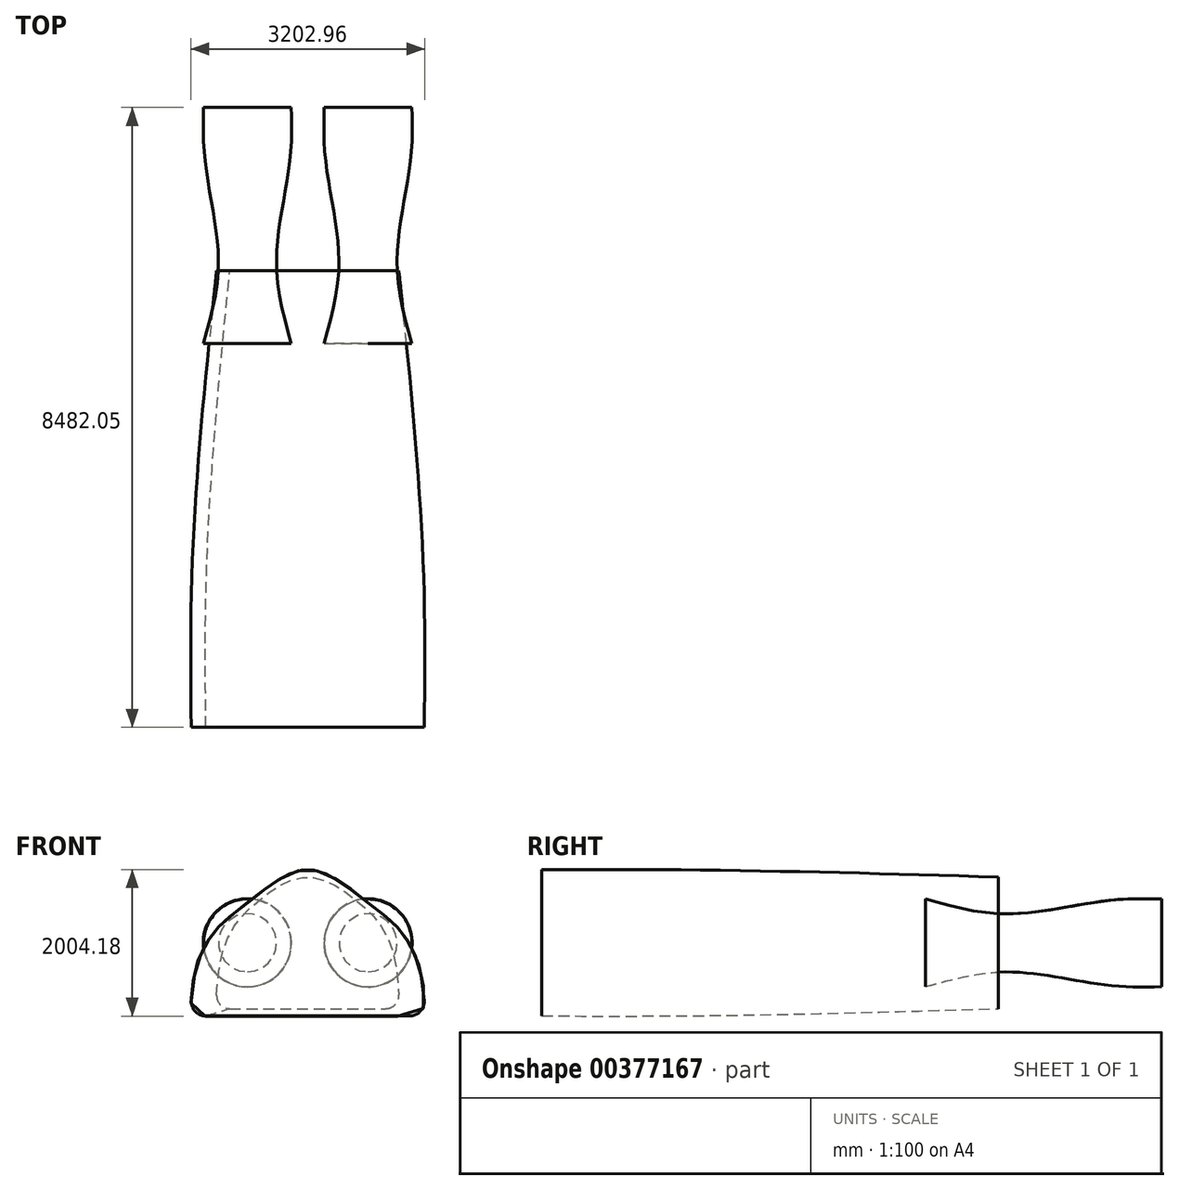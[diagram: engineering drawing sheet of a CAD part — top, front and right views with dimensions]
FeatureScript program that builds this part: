
annotation { "Feature Type Name" : "Feature", "Feature Type Description" : "" }
export const myFeature = defineFeature(function(context is Context, id is Id, definition is map)
    precondition{}
    {
        {
            var Q0;
            Q0=qCreatedBy(makeId("Front.planeOp"),FACE);
            cPlane(context, id + "F0", {"entities" : qUnion([Q0]), "cplaneType" : CPlaneType.OFFSET, "offset" : 1750 * mm, "width" : 150 * mm, "height" : 150 * mm});
        }
        {
            var Q0;
            Q0=qCreatedBy(id+"F0.planeOp",FACE);
            var sketch = newSketch(context, id + "F1", { "sketchPlane" : qUnion([Q0])});
            skLineSegment(sketch, "E0.top", {"start": v(-1394.2, -1000) * mm, "end": v(1394.2, -1000) * mm});
            skPoint(sketch, "E0.middle", {"position": v(0, 0) * mm});
            skFitSpline(sketch, "E1", {"points": [v(-1600, -1000) * mm, v(-848, 530) * mm, v(0, 1000) * mm, v(848, 530) * mm, v(1600, -1000) * mm], "startDerivative": vector(0, 10524.75) * mm, "endDerivative": vector(0, -10524.75) * mm});
            skArc(sketch, "E2.filletArc", {"start": v(-1593.82, -787.83) * mm, "mid": v(-1539.85, -937.05) * mm, "end": v(-1394.2, -1000) * mm});
            skArc(sketch, "E3.filletArc", {"start": v(1394.2, -1000) * mm, "mid": v(1539.85, -937.05) * mm, "end": v(1593.82, -787.83) * mm});
            skSolve(sketch);
        }
        {
            var Q0;
            Q0=qCreatedBy(makeId("Front.planeOp"),FACE);
            var sketch = newSketch(context, id + "F2", { "sketchPlane" : qUnion([Q0])});
            skLineSegment(sketch, "E4.top", {"start": v(-1394.2, -1000) * mm, "end": v(1394.2, -1000) * mm});
            skPoint(sketch, "E4.middle", {"position": v(0, 0) * mm});
            skFitSpline(sketch, "E5", {"points": [v(-1600, -1000) * mm, v(-848, 530) * mm, v(0, 1000) * mm, v(848, 530) * mm, v(1600, -1000) * mm], "startDerivative": vector(0, 10524.75) * mm, "endDerivative": vector(0, -10524.75) * mm});
            skArc(sketch, "E6.filletArc", {"start": v(-1593.82, -787.83) * mm, "mid": v(-1539.85, -937.05) * mm, "end": v(-1394.2, -1000) * mm});
            skArc(sketch, "E7.filletArc", {"start": v(1394.2, -1000) * mm, "mid": v(1539.85, -937.05) * mm, "end": v(1593.82, -787.83) * mm});
            skSolve(sketch);
        }
        {
            var Q0;
            Q0=qCreatedBy(makeId("Front.planeOp"),FACE);
            cPlane(context, id + "F3", {"entities" : qUnion([Q0]), "cplaneType" : CPlaneType.OFFSET, "offset" : 3500 * mm, "oppositeDirection" : true, "width" : 150 * mm, "height" : 150 * mm});
        }
        {
            var Q0;
            Q0=qCreatedBy(id+"F3.planeOp",FACE);
            var sketch = newSketch(context, id + "F4", { "sketchPlane" : qUnion([Q0])});
            skLineSegment(sketch, "E8.top", {"start": v(-1066.5, -800) * mm, "end": v(1066.5, -800) * mm});
            skPoint(sketch, "E8.middle", {"position": v(0, 0) * mm});
            skFitSpline(sketch, "E9", {"points": [v(-1250, -800) * mm, v(-775.25, 631.66) * mm, v(0, 1000) * mm, v(775.25, 631.66) * mm, v(1250, -800) * mm], "startDerivative": vector(0, 8420.89) * mm, "endDerivative": vector(0, -8420.89) * mm});
            skArc(sketch, "E10.filletArc", {"start": v(-1246.34, -612.7) * mm, "mid": v(-1196.33, -744.67) * mm, "end": v(-1066.5, -800) * mm});
            skArc(sketch, "E11.filletArc", {"start": v(1066.5, -800) * mm, "mid": v(1196.33, -744.67) * mm, "end": v(1246.34, -612.7) * mm});
            skSolve(sketch);
        }
        {
            var Q0;
            Q0=qCreatedBy(makeId("Front.planeOp"),FACE);
            cPlane(context, id + "F5", {"entities" : qUnion([Q0]), "cplaneType" : CPlaneType.OFFSET, "offset" : 4500 * mm, "oppositeDirection" : true, "width" : 150 * mm, "height" : 150 * mm});
        }
        {
            var Q0;
            Q0=qCreatedBy(id+"F5.planeOp",FACE);
            var sketch = newSketch(context, id + "F6", { "sketchPlane" : qUnion([Q0])});
            skLineSegment(sketch, "E12.top", {"start": v(-1066.63, -900) * mm, "end": v(1066.63, -900) * mm});
            skPoint(sketch, "E12.middle", {"position": v(0, 0) * mm});
            skFitSpline(sketch, "E13", {"points": [v(-1250, -900) * mm, v(-730.38, 525.87) * mm, v(0, 900) * mm, v(730.38, 525.87) * mm, v(1250, -900) * mm], "startDerivative": vector(0, 9370.88) * mm, "endDerivative": vector(0, -9370.88) * mm});
            skArc(sketch, "E14.filletArc", {"start": v(-1246.49, -712.94) * mm, "mid": v(-1196.38, -844.76) * mm, "end": v(-1066.63, -900) * mm});
            skArc(sketch, "E15.filletArc", {"start": v(1066.63, -900) * mm, "mid": v(1196.38, -844.76) * mm, "end": v(1246.49, -712.94) * mm});
            skSolve(sketch);
        }
        {
            var Q0;
            Q0=qCreatedBy(makeId("Front.planeOp"),FACE);
            cPlane(context, id + "F7", {"entities" : qUnion([Q0]), "cplaneType" : CPlaneType.OFFSET, "offset" : 6232.05 * mm, "oppositeDirection" : true, "width" : 150 * mm, "height" : 150 * mm});
        }
        {
            var Q0;
            Q0=makeQuery(id+"F1.imprint","IMPRINT",FACE,{"disambiguationData":[TD([[makeQuery(id+"F1.imprint","IMPRINT",EDGE,{"derivedFrom":sQuery(id+"F1.wireOp",EDGE,"E0.top")}),1.0]])]});
            var Q1;
            Q1=makeQuery(id+"F2.imprint","IMPRINT",FACE,{"disambiguationData":[TD([[makeQuery(id+"F2.imprint","IMPRINT",EDGE,{"derivedFrom":sQuery(id+"F2.wireOp",EDGE,"E4.top")}),1.0]])]});
            var Q2;
            Q2=makeQuery(id+"F6.imprint","IMPRINT",FACE,{"disambiguationData":[TD([[makeQuery(id+"F6.imprint","IMPRINT",EDGE,{"derivedFrom":sQuery(id+"F6.wireOp",EDGE,"E12.top")}),1.0]])]});
            loft(context, id + "F8", {"sheetProfilesArray" : [{ "sheetProfileEntities" : qUnion([Q0]) }, { "sheetProfileEntities" : qUnion([Q1]) }, { "sheetProfileEntities" : qUnion([Q2]) }]});
        }
        {
            var Q0;
            Q0=qCreatedBy(makeId("Front.planeOp"),FACE);
            cPlane(context, id + "F9", {"entities" : qUnion([Q0]), "cplaneType" : CPlaneType.OFFSET, "offset" : 3500 * mm, "oppositeDirection" : true, "width" : 150 * mm, "height" : 150 * mm});
        }
        {
            var Q0;
            Q0=qCreatedBy(id+"F9.planeOp",FACE);
            var sketch = newSketch(context, id + "F10", { "sketchPlane" : qUnion([Q0])});
            skPoint(sketch, "E16.endSnap0", {"position": v(-412.5, 0) * mm});
            skCircle(sketch, "E17", {"center": v(-825, 0) * mm, "radius": 600 * mm});
            skCircle(sketch, "E18", {"center": v(825, 0) * mm, "radius": 600 * mm});
            skSolve(sketch);
        }
        {
            var Q0;
            Q0=qCreatedBy(makeId("Front.planeOp"),FACE);
            cPlane(context, id + "F11", {"entities" : qUnion([Q0]), "cplaneType" : CPlaneType.OFFSET, "offset" : 4500 * mm, "oppositeDirection" : true, "width" : 150 * mm, "height" : 150 * mm});
        }
        {
            var Q0;
            Q0=qCreatedBy(id+"F11.planeOp",FACE);
            var sketch = newSketch(context, id + "F12", { "sketchPlane" : qUnion([Q0])});
            skCircle(sketch, "E19", {"center": v(-825, 0) * mm, "radius": 400 * mm});
            skCircle(sketch, "E20", {"center": v(825, 0) * mm, "radius": 400 * mm});
            skSolve(sketch);
        }
        {
            var Q0;
            Q0=qCreatedBy(makeId("Front.planeOp"),FACE);
            cPlane(context, id + "F13", {"entities" : qUnion([Q0]), "cplaneType" : CPlaneType.OFFSET, "offset" : 6232.05 * mm, "oppositeDirection" : true, "width" : 150 * mm, "height" : 150 * mm});
        }
        {
            var Q0;
            Q0=qCreatedBy(id+"F13.planeOp",FACE);
            var sketch = newSketch(context, id + "F14", { "sketchPlane" : qUnion([Q0])});
            skCircle(sketch, "E21", {"center": v(-825, 0) * mm, "radius": 600 * mm});
            skCircle(sketch, "E22", {"center": v(825, 0) * mm, "radius": 600 * mm});
            skSolve(sketch);
        }
        {
            var Q0;
            Q0=qCreatedBy(makeId("Front.planeOp"),FACE);
            cPlane(context, id + "F15", {"entities" : qUnion([Q0]), "cplaneType" : CPlaneType.OFFSET, "offset" : 6732.05 * mm, "oppositeDirection" : true, "width" : 150 * mm, "height" : 150 * mm});
        }
        {
            var Q0;
            Q0=qCreatedBy(id+"F15.planeOp",FACE);
            var sketch = newSketch(context, id + "F16", { "sketchPlane" : qUnion([Q0])});
            skCircle(sketch, "E23", {"center": v(-825, 0) * mm, "radius": 600 * mm});
            skCircle(sketch, "E24", {"center": v(825, 0) * mm, "radius": 600 * mm});
            skSolve(sketch);
        }
        {
            var Q1;
            Q1=makeQuery(id+"F10.imprint","IMPRINT",FACE,{"disambiguationData":[TD([[makeQuery(id+"F10.imprint","IMPRINT",EDGE,{"derivedFrom":sQuery(id+"F10.wireOp",EDGE,"E17")}),1.0]])]});
            var Q2;
            Q2=makeQuery(id+"F12.imprint","IMPRINT",FACE,{"disambiguationData":[TD([[makeQuery(id+"F12.imprint","IMPRINT",EDGE,{"derivedFrom":sQuery(id+"F12.wireOp",EDGE,"E19")}),1.0]])]});
            var Q3;
            Q3=makeQuery(id+"F14.imprint","IMPRINT",FACE,{"disambiguationData":[TD([[makeQuery(id+"F14.imprint","IMPRINT",EDGE,{"derivedFrom":sQuery(id+"F14.wireOp",EDGE,"E21")}),1.0]])]});
            var Q4;
            Q4=makeQuery(id+"F16.imprint","IMPRINT",FACE,{"disambiguationData":[TD([[makeQuery(id+"F16.imprint","IMPRINT",EDGE,{"derivedFrom":sQuery(id+"F16.wireOp",EDGE,"E23")}),1.0]])]});
            loft(context, id + "F17", {"sheetProfilesArray" : [{ "sheetProfileEntities" : qUnion([Q1]) }, { "sheetProfileEntities" : qUnion([Q2]) }, { "sheetProfileEntities" : qUnion([Q3]) }, { "sheetProfileEntities" : qUnion([Q4]) }]});
        }
        {
            var Q1;
            Q1=makeQuery(id+"F10.imprint","IMPRINT",FACE,{"disambiguationData":[TD([[makeQuery(id+"F10.imprint","IMPRINT",EDGE,{"derivedFrom":sQuery(id+"F10.wireOp",EDGE,"E18")}),1.0]])]});
            var Q2;
            Q2=makeQuery(id+"F12.imprint","IMPRINT",FACE,{"disambiguationData":[TD([[makeQuery(id+"F12.imprint","IMPRINT",EDGE,{"derivedFrom":sQuery(id+"F12.wireOp",EDGE,"E20")}),1.0]])]});
            var Q3;
            Q3=makeQuery(id+"F14.imprint","IMPRINT",FACE,{"disambiguationData":[TD([[makeQuery(id+"F14.imprint","IMPRINT",EDGE,{"derivedFrom":sQuery(id+"F14.wireOp",EDGE,"E22")}),1.0]])]});
            var Q4;
            Q4=makeQuery(id+"F16.imprint","IMPRINT",FACE,{"disambiguationData":[TD([[makeQuery(id+"F16.imprint","IMPRINT",EDGE,{"derivedFrom":sQuery(id+"F16.wireOp",EDGE,"E24")}),1.0]])]});
            loft(context, id + "F18", {"sheetProfilesArray" : [{ "sheetProfileEntities" : qUnion([Q1]) }, { "sheetProfileEntities" : qUnion([Q2]) }, { "sheetProfileEntities" : qUnion([Q3]) }, { "sheetProfileEntities" : qUnion([Q4]) }]});
        }
    });
